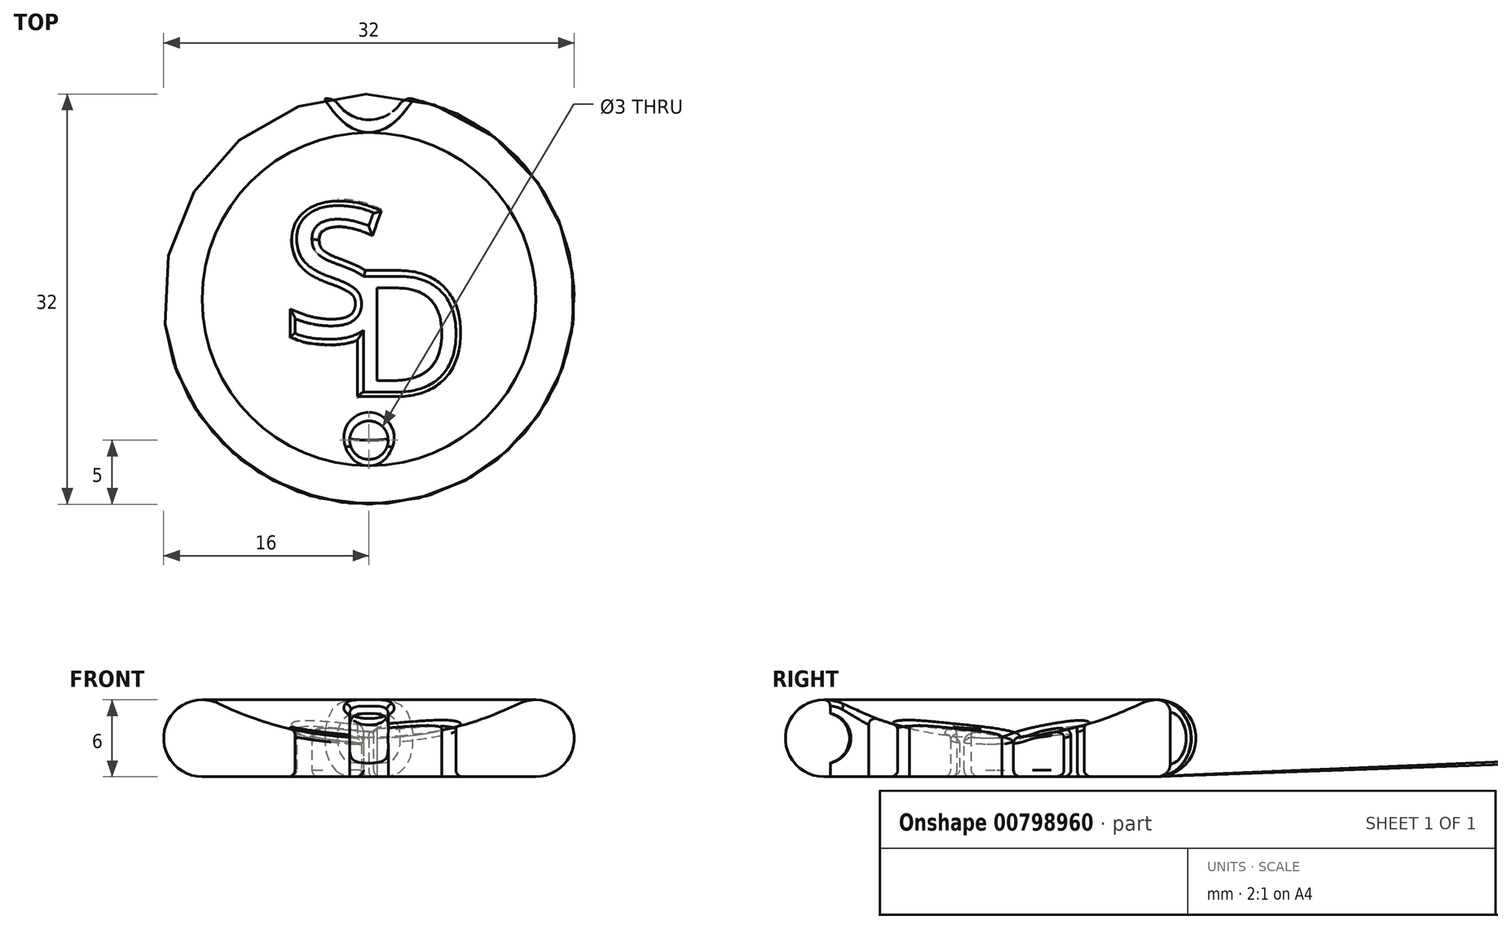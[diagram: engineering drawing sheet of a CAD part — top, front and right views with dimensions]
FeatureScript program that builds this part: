
annotation { "Feature Type Name" : "Feature", "Feature Type Description" : "" }
export const myFeature = defineFeature(function(context is Context, id is Id, definition is map)
    precondition{}
    {
        {
            var Q0;
            Q0=qCreatedBy(makeId("Front.planeOp"),FACE);
            var sketch = newSketch(context, id + "F0", { "sketchPlane" : qUnion([Q0])});
            skArc(sketch, "E0", {"start": v(-11.69, 5.7) * mm, "mid": v(-15.92, 3.67) * mm, "end": v(-13, 0) * mm});
            skArc(sketch, "E1", {"start": v(-11.69, 5.7) * mm, "mid": v(-6, 3.68) * mm, "end": v(0, 3) * mm});
            skLineSegment(sketch, "E2", {"start": v(-13, 0) * mm, "end": v(0, 0) * mm});
            skLineSegment(sketch, "E3", {"start": v(0, 0) * mm, "end": v(0, 3) * mm});
            skSolve(sketch);
        }
        {
            var Q0;
            Q0=makeQuery(id+"F0.imprint","IMPRINT",FACE,{"disambiguationData":[TD([[makeQuery(id+"F0.imprint","IMPRINT",EDGE,{"derivedFrom":sQuery(id+"F0.wireOp",EDGE,"E0")}),1.0]])]});
            var Q1;
            Q1=sQuery(id+"F0.wireOp",EDGE,"E3");
            revolve(context, id + "F1", {"surfaceOperationType" : NewSurfaceOperationType.NEW, "entities" : qUnion([Q0]), "axis" : qUnion([Q1]), "revolveType" : RevolveType.FULL});
        }
        {
            var Q0;
            Q0=qCreatedBy(makeId("Top.planeOp"),FACE);
            var sketch = newSketch(context, id + "F2", { "sketchPlane" : qUnion([Q0])});
            skCircle(sketch, "E4", {"center": v(0, 17) * mm, "radius": 3 * mm});
            skSolve(sketch);
        }
        {
            var Q0;
            Q0=qCreatedBy(makeId("Front.planeOp"),FACE);
            var sketch = newSketch(context, id + "F3", { "sketchPlane" : qUnion([Q0])});
            skCircle(sketch, "E5", {"center": v(-13, 3) * mm, "radius": 2 * mm});
            skSolve(sketch);
        }
        {
            var Q0;
            Q0=qCreatedBy(makeId("Top.planeOp"),FACE);
            var sketch = newSketch(context, id + "F4", { "sketchPlane" : qUnion([Q0])});
            skCircle(sketch, "E6", {"center": v(0, -11) * mm, "radius": 1.5 * mm});
            skSolve(sketch);
        }
        {
            var Q0;
            Q0=qSketchRegion(id+"F4",true);
            extrude(context, id + "F5", {"entities" : qUnion([Q0]), "operationType" : NewBodyOperationType.REMOVE, "depth" : 6 * mm, "offsetDistance" : 25 * mm});
        }
        {
            var Q0;
            Q0=makeQuery(id+"F5.boolean.opBoolean","INTERSECT",EDGE,{"derivedFrom":[makeQuery(id+"F1.opRevolve","SWEPT_FACE",FACE,{"disambiguationData":[OSD([sQuery(id+"F0.wireOp",EDGE,"E1")])]}),makeQuery(id+"F5.opExtrude","SWEPT_FACE",FACE,{"disambiguationData":[OSD([sQuery(id+"F4.wireOp",EDGE,"E6")])]})]});
            var Q1;
            Q1=makeQuery(id+"F5.boolean.opBoolean","INTERSECT",EDGE,{"derivedFrom":[makeQuery(id+"F1.opRevolve","SWEPT_FACE",FACE,{"disambiguationData":[OSD([sQuery(id+"F0.wireOp",EDGE,"E0")])]}),makeQuery(id+"F5.opExtrude","SWEPT_FACE",FACE,{"disambiguationData":[OSD([sQuery(id+"F4.wireOp",EDGE,"E6")])]})]});
            var Q2;
            Q2=makeQuery(id+"F5.boolean.opBoolean","COPY",EDGE,{"derivedFrom":makeQuery(id+"F5.opExtrude","CAP_EDGE",EDGE,{"disambiguationData":[OSD([sQuery(id+"F4.wireOp",EDGE,"E6")])],"isStart":true})});
            fillet(context, id + "F6", {"entities" : qUnion([Q0, Q1, Q2]), "radius" : 0.5 * mm, "tangentPropagation" : true, "allowEdgeOverflow" : false});
        }
        {
            var Q0;
            Q0=qSketchRegion(id+"F3",true);
            var Q1;
            Q1=sQuery(id+"F0.wireOp",EDGE,"E3");
            revolve(context, id + "F7", {"operationType" : NewBodyOperationType.ADD, "surfaceOperationType" : NewSurfaceOperationType.NEW, "entities" : qUnion([Q0]), "axis" : qUnion([Q1]), "revolveType" : RevolveType.FULL});
        }
        {
            var Q0;
            Q0=qSketchRegion(id+"F2",true);
            extrude(context, id + "F8", {"entities" : qUnion([Q0]), "operationType" : NewBodyOperationType.REMOVE, "depth" : 6 * mm, "offsetDistance" : 25 * mm});
        }
        {
            var Q0;
            Q0=makeQuery(id+"F8.boolean.opBoolean","INTERSECT",EDGE,{"derivedFrom":[makeQuery(id+"F1.opRevolve","SWEPT_FACE",FACE,{"disambiguationData":[OSD([sQuery(id+"F0.wireOp",EDGE,"E0")])]}),makeQuery(id+"F8.opExtrude","SWEPT_FACE",FACE,{"disambiguationData":[OSD([sQuery(id+"F2.wireOp",EDGE,"E4")])]})]});
            fillet(context, id + "F9", {"entities" : qUnion([Q0]), "radius" : 1 * mm, "tangentPropagation" : true, "allowEdgeOverflow" : false});
        }
        {
            var Q0;
            Q0=qCreatedBy(makeId("Top.planeOp"),FACE);
            var sketch = newSketch(context, id + "F10", { "sketchPlane" : qUnion([Q0])});
            skText(sketch, "E7", { "text": "S", "fontName": "OpenSans-Regular.ttf"});
            skText(sketch, "E8", { "text": "D", "fontName": "OpenSans-Regular.ttf"});
            const initialGuessF10  = {"E7": [-0.0065, -0.00298, 1, 0, 0.01022], "E8": [-0.00167, -0.00725, 1, 0, 0.00911]};
            skSetInitialGuess(sketch, initialGuessF10);
            skSolve(sketch);
        }
        {
            var Q0;
            Q0=qSketchRegion(id+"F10",true);
            extrude(context, id + "F11", {"entities" : qUnion([Q0]), "operationType" : NewBodyOperationType.REMOVE, "depth" : 6 * mm, "offsetDistance" : 25 * mm});
        }
        {
            var Q0;
            Q0=makeQuery(id+"F11.boolean.opBoolean","INTERSECT",EDGE,{"derivedFrom":[makeQuery(id+"F1.opRevolve","SWEPT_FACE",FACE,{"disambiguationData":[OSD([sQuery(id+"F0.wireOp",EDGE,"E1")])]}),makeQuery(id+"F11.opExtrude","SWEPT_FACE",FACE,{"disambiguationData":[OSD([sQuery(id+"F10.wireOp",EDGE,"E7.sketch_text.stroke-7")])]})]});
            var Q1;
            Q1=makeQuery(id+"F11.boolean.opBoolean","INTERSECT",EDGE,{"derivedFrom":[makeQuery(id+"F1.opRevolve","SWEPT_FACE",FACE,{"disambiguationData":[OSD([sQuery(id+"F0.wireOp",EDGE,"E1")])]}),makeQuery(id+"F11.opExtrude","SWEPT_FACE",FACE,{"disambiguationData":[OSD([sQuery(id+"F10.wireOp",EDGE,"E7.sketch_text.stroke-6")])]})]});
            var Q2;
            Q2=makeQuery(id+"F11.boolean.opBoolean","INTERSECT",EDGE,{"derivedFrom":[makeQuery(id+"F1.opRevolve","SWEPT_FACE",FACE,{"disambiguationData":[OSD([sQuery(id+"F0.wireOp",EDGE,"E1")])]}),makeQuery(id+"F11.opExtrude","SWEPT_FACE",FACE,{"disambiguationData":[OSD([sQuery(id+"F10.wireOp",EDGE,"E7.sketch_text.stroke-4")])]})]});
            var Q3;
            Q3=makeQuery(id+"F11.boolean.opBoolean","INTERSECT",EDGE,{"derivedFrom":[makeQuery(id+"F1.opRevolve","SWEPT_FACE",FACE,{"disambiguationData":[OSD([sQuery(id+"F0.wireOp",EDGE,"E1")])]}),makeQuery(id+"F11.opExtrude","SWEPT_FACE",FACE,{"disambiguationData":[OSD([sQuery(id+"F10.wireOp",EDGE,"E7.sketch_text.stroke-5")])]})]});
            var Q4;
            Q4=makeQuery(id+"F11.boolean.opBoolean","INTERSECT",EDGE,{"derivedFrom":[makeQuery(id+"F1.opRevolve","SWEPT_FACE",FACE,{"disambiguationData":[OSD([sQuery(id+"F0.wireOp",EDGE,"E1")])]}),makeQuery(id+"F11.opExtrude","SWEPT_FACE",FACE,{"disambiguationData":[OSD([sQuery(id+"F10.wireOp",EDGE,"E7.sketch_text.stroke-3")])]})]});
            var Q5;
            Q5=makeQuery(id+"F11.boolean.opBoolean","INTERSECT",EDGE,{"derivedFrom":[makeQuery(id+"F1.opRevolve","SWEPT_FACE",FACE,{"disambiguationData":[OSD([sQuery(id+"F0.wireOp",EDGE,"E1")])]}),makeQuery(id+"F11.opExtrude","SWEPT_FACE",FACE,{"disambiguationData":[OSD([sQuery(id+"F10.wireOp",EDGE,"E7.sketch_text.stroke-2")])]})]});
            var Q6;
            Q6=makeQuery(id+"F11.boolean.opBoolean","INTERSECT",EDGE,{"derivedFrom":[makeQuery(id+"F1.opRevolve","SWEPT_FACE",FACE,{"disambiguationData":[OSD([sQuery(id+"F0.wireOp",EDGE,"E1")])]}),makeQuery(id+"F11.opExtrude","SWEPT_FACE",FACE,{"disambiguationData":[OSD([sQuery(id+"F10.wireOp",EDGE,"E7.sketch_text.stroke-1")])]})]});
            var Q7;
            Q7=makeQuery(id+"F11.boolean.opBoolean","INTERSECT",EDGE,{"derivedFrom":[makeQuery(id+"F1.opRevolve","SWEPT_FACE",FACE,{"disambiguationData":[OSD([sQuery(id+"F0.wireOp",EDGE,"E1")])]}),makeQuery(id+"F11.opExtrude","SWEPT_FACE",FACE,{"disambiguationData":[OSD([sQuery(id+"F10.wireOp",EDGE,"E8.sketch_text.stroke-3")])]})]});
            var Q8;
            Q8=makeQuery(id+"F11.boolean.opBoolean","INTERSECT",EDGE,{"derivedFrom":[makeQuery(id+"F1.opRevolve","SWEPT_FACE",FACE,{"disambiguationData":[OSD([sQuery(id+"F0.wireOp",EDGE,"E1")])]}),makeQuery(id+"F11.opExtrude","SWEPT_FACE",FACE,{"disambiguationData":[OSD([sQuery(id+"F10.wireOp",EDGE,"E8.sketch_text.stroke-2")])]})]});
            var Q9;
            Q9=makeQuery(id+"F11.boolean.opBoolean","INTERSECT",EDGE,{"derivedFrom":[makeQuery(id+"F1.opRevolve","SWEPT_FACE",FACE,{"disambiguationData":[OSD([sQuery(id+"F0.wireOp",EDGE,"E1")])]}),makeQuery(id+"F11.opExtrude","SWEPT_FACE",FACE,{"disambiguationData":[OSD([sQuery(id+"F10.wireOp",EDGE,"E8.sketch_text.stroke-1")])]})]});
            var Q10;
            Q10=makeQuery(id+"F11.boolean.opBoolean","INTERSECT",EDGE,{"derivedFrom":[makeQuery(id+"F1.opRevolve","SWEPT_FACE",FACE,{"disambiguationData":[OSD([sQuery(id+"F0.wireOp",EDGE,"E1")])]}),makeQuery(id+"F11.opExtrude","SWEPT_FACE",FACE,{"disambiguationData":[OSD([sQuery(id+"F10.wireOp",EDGE,"E8.sketch_text.stroke-0")])]})]});
            var Q11;
            Q11=makeQuery(id+"F11.boolean.opBoolean","INTERSECT",EDGE,{"derivedFrom":[makeQuery(id+"F1.opRevolve","SWEPT_FACE",FACE,{"disambiguationData":[OSD([sQuery(id+"F0.wireOp",EDGE,"E1")])]}),makeQuery(id+"F11.opExtrude","SWEPT_FACE",FACE,{"disambiguationData":[OSD([sQuery(id+"F10.wireOp",EDGE,"E8.sketch_text.stroke-6")])]})]});
            var Q12;
            Q12=makeQuery(id+"F11.boolean.opBoolean","INTERSECT",EDGE,{"derivedFrom":[makeQuery(id+"F1.opRevolve","SWEPT_FACE",FACE,{"disambiguationData":[OSD([sQuery(id+"F0.wireOp",EDGE,"E1")])]}),makeQuery(id+"F11.opExtrude","SWEPT_FACE",FACE,{"disambiguationData":[OSD([sQuery(id+"F10.wireOp",EDGE,"E8.sketch_text.stroke-5")])]})]});
            var Q13;
            Q13=makeQuery(id+"F11.boolean.opBoolean","INTERSECT",EDGE,{"derivedFrom":[makeQuery(id+"F1.opRevolve","SWEPT_FACE",FACE,{"disambiguationData":[OSD([sQuery(id+"F0.wireOp",EDGE,"E1")])]}),makeQuery(id+"F11.opExtrude","SWEPT_FACE",FACE,{"disambiguationData":[OSD([sQuery(id+"F10.wireOp",EDGE,"E8.sketch_text.stroke-4")])]})]});
            var Q14;
            Q14=makeQuery(id+"F11.boolean.opBoolean","INTERSECT",EDGE,{"derivedFrom":[makeQuery(id+"F1.opRevolve","SWEPT_FACE",FACE,{"disambiguationData":[OSD([sQuery(id+"F0.wireOp",EDGE,"E1")])]}),makeQuery(id+"F11.opExtrude","SWEPT_FACE",FACE,{"disambiguationData":[OSD([sQuery(id+"F10.wireOp",EDGE,"E7.sketch_text.stroke-24")])]})]});
            var Q15;
            Q15=makeQuery(id+"F11.boolean.opBoolean","INTERSECT",EDGE,{"derivedFrom":[makeQuery(id+"F1.opRevolve","SWEPT_FACE",FACE,{"disambiguationData":[OSD([sQuery(id+"F0.wireOp",EDGE,"E1")])]}),makeQuery(id+"F11.opExtrude","SWEPT_FACE",FACE,{"disambiguationData":[OSD([sQuery(id+"F10.wireOp",EDGE,"E7.sketch_text.stroke-23")])]})]});
            var Q16;
            Q16=makeQuery(id+"F11.boolean.opBoolean","INTERSECT",EDGE,{"derivedFrom":[makeQuery(id+"F1.opRevolve","SWEPT_FACE",FACE,{"disambiguationData":[OSD([sQuery(id+"F0.wireOp",EDGE,"E1")])]}),makeQuery(id+"F11.opExtrude","SWEPT_FACE",FACE,{"disambiguationData":[OSD([sQuery(id+"F10.wireOp",EDGE,"E7.sketch_text.stroke-22")])]})]});
            var Q17;
            Q17=makeQuery(id+"F11.boolean.opBoolean","INTERSECT",EDGE,{"derivedFrom":[makeQuery(id+"F1.opRevolve","SWEPT_FACE",FACE,{"disambiguationData":[OSD([sQuery(id+"F0.wireOp",EDGE,"E1")])]}),makeQuery(id+"F11.opExtrude","SWEPT_FACE",FACE,{"disambiguationData":[OSD([sQuery(id+"F10.wireOp",EDGE,"E7.sketch_text.stroke-21")])]})]});
            var Q18;
            Q18=makeQuery(id+"F11.boolean.opBoolean","INTERSECT",EDGE,{"derivedFrom":[makeQuery(id+"F1.opRevolve","SWEPT_FACE",FACE,{"disambiguationData":[OSD([sQuery(id+"F0.wireOp",EDGE,"E1")])]}),makeQuery(id+"F11.opExtrude","SWEPT_FACE",FACE,{"disambiguationData":[OSD([sQuery(id+"F10.wireOp",EDGE,"E7.sketch_text.stroke-20")])]})]});
            var Q19;
            Q19=makeQuery(id+"F11.boolean.opBoolean","INTERSECT",EDGE,{"derivedFrom":[makeQuery(id+"F1.opRevolve","SWEPT_FACE",FACE,{"disambiguationData":[OSD([sQuery(id+"F0.wireOp",EDGE,"E1")])]}),makeQuery(id+"F11.opExtrude","SWEPT_FACE",FACE,{"disambiguationData":[OSD([sQuery(id+"F10.wireOp",EDGE,"E7.sketch_text.stroke-19")])]})]});
            var Q20;
            Q20=makeQuery(id+"F11.boolean.opBoolean","INTERSECT",EDGE,{"derivedFrom":[makeQuery(id+"F1.opRevolve","SWEPT_FACE",FACE,{"disambiguationData":[OSD([sQuery(id+"F0.wireOp",EDGE,"E1")])]}),makeQuery(id+"F11.opExtrude","SWEPT_FACE",FACE,{"disambiguationData":[OSD([sQuery(id+"F10.wireOp",EDGE,"E7.sketch_text.stroke-18")])]})]});
            var Q21;
            Q21=makeQuery(id+"F11.boolean.opBoolean","INTERSECT",EDGE,{"derivedFrom":[makeQuery(id+"F1.opRevolve","SWEPT_FACE",FACE,{"disambiguationData":[OSD([sQuery(id+"F0.wireOp",EDGE,"E1")])]}),makeQuery(id+"F11.opExtrude","SWEPT_FACE",FACE,{"disambiguationData":[OSD([sQuery(id+"F10.wireOp",EDGE,"E7.sketch_text.stroke-17")])]})]});
            var Q22;
            Q22=makeQuery(id+"F11.boolean.opBoolean","INTERSECT",EDGE,{"derivedFrom":[makeQuery(id+"F1.opRevolve","SWEPT_FACE",FACE,{"disambiguationData":[OSD([sQuery(id+"F0.wireOp",EDGE,"E1")])]}),makeQuery(id+"F11.opExtrude","SWEPT_FACE",FACE,{"disambiguationData":[OSD([sQuery(id+"F10.wireOp",EDGE,"E7.sketch_text.stroke-16")])]})]});
            var Q23;
            Q23=makeQuery(id+"F11.boolean.opBoolean","INTERSECT",EDGE,{"derivedFrom":[makeQuery(id+"F1.opRevolve","SWEPT_FACE",FACE,{"disambiguationData":[OSD([sQuery(id+"F0.wireOp",EDGE,"E1")])]}),makeQuery(id+"F11.opExtrude","SWEPT_FACE",FACE,{"disambiguationData":[OSD([sQuery(id+"F10.wireOp",EDGE,"E7.sketch_text.stroke-15")])]})]});
            var Q24;
            Q24=makeQuery(id+"F11.boolean.opBoolean","INTERSECT",EDGE,{"derivedFrom":[makeQuery(id+"F1.opRevolve","SWEPT_FACE",FACE,{"disambiguationData":[OSD([sQuery(id+"F0.wireOp",EDGE,"E1")])]}),makeQuery(id+"F11.opExtrude","SWEPT_FACE",FACE,{"disambiguationData":[OSD([sQuery(id+"F10.wireOp",EDGE,"E7.sketch_text.stroke-14")])]})]});
            var Q25;
            Q25=makeQuery(id+"F11.boolean.opBoolean","INTERSECT",EDGE,{"derivedFrom":[makeQuery(id+"F1.opRevolve","SWEPT_FACE",FACE,{"disambiguationData":[OSD([sQuery(id+"F0.wireOp",EDGE,"E1")])]}),makeQuery(id+"F11.opExtrude","SWEPT_FACE",FACE,{"disambiguationData":[OSD([sQuery(id+"F10.wireOp",EDGE,"E7.sketch_text.stroke-13")])]})]});
            var Q26;
            Q26=makeQuery(id+"F11.boolean.opBoolean","INTERSECT",EDGE,{"derivedFrom":[makeQuery(id+"F1.opRevolve","SWEPT_FACE",FACE,{"disambiguationData":[OSD([sQuery(id+"F0.wireOp",EDGE,"E1")])]}),makeQuery(id+"F11.opExtrude","SWEPT_FACE",FACE,{"disambiguationData":[OSD([sQuery(id+"F10.wireOp",EDGE,"E7.sketch_text.stroke-12")])]})]});
            var Q27;
            Q27=makeQuery(id+"F11.boolean.opBoolean","INTERSECT",EDGE,{"derivedFrom":[makeQuery(id+"F1.opRevolve","SWEPT_FACE",FACE,{"disambiguationData":[OSD([sQuery(id+"F0.wireOp",EDGE,"E1")])]}),makeQuery(id+"F11.opExtrude","SWEPT_FACE",FACE,{"disambiguationData":[OSD([sQuery(id+"F10.wireOp",EDGE,"E7.sketch_text.stroke-11")])]})]});
            var Q28;
            Q28=makeQuery(id+"F11.boolean.opBoolean","INTERSECT",EDGE,{"derivedFrom":[makeQuery(id+"F1.opRevolve","SWEPT_FACE",FACE,{"disambiguationData":[OSD([sQuery(id+"F0.wireOp",EDGE,"E1")])]}),makeQuery(id+"F11.opExtrude","SWEPT_FACE",FACE,{"disambiguationData":[OSD([sQuery(id+"F10.wireOp",EDGE,"E7.sketch_text.stroke-10")])]})]});
            var Q29;
            Q29=makeQuery(id+"F11.boolean.opBoolean","INTERSECT",EDGE,{"derivedFrom":[makeQuery(id+"F1.opRevolve","SWEPT_FACE",FACE,{"disambiguationData":[OSD([sQuery(id+"F0.wireOp",EDGE,"E1")])]}),makeQuery(id+"F11.opExtrude","SWEPT_FACE",FACE,{"disambiguationData":[OSD([sQuery(id+"F10.wireOp",EDGE,"E7.sketch_text.stroke-9")])]})]});
            var Q30;
            Q30=makeQuery(id+"F11.boolean.opBoolean","INTERSECT",EDGE,{"derivedFrom":[makeQuery(id+"F1.opRevolve","SWEPT_FACE",FACE,{"disambiguationData":[OSD([sQuery(id+"F0.wireOp",EDGE,"E1")])]}),makeQuery(id+"F11.opExtrude","SWEPT_FACE",FACE,{"disambiguationData":[OSD([sQuery(id+"F10.wireOp",EDGE,"E7.sketch_text.stroke-8")])]})]});
            var Q31;
            Q31=makeQuery(id+"F11.boolean.opBoolean","COPY",EDGE,{"derivedFrom":makeQuery(id+"F11.opExtrude","CAP_EDGE",EDGE,{"disambiguationData":[OSD([sQuery(id+"F10.wireOp",EDGE,"E8.sketch_text.stroke-3")])],"isStart":true})});
            var Q32;
            Q32=makeQuery(id+"F11.boolean.opBoolean","COPY",EDGE,{"derivedFrom":makeQuery(id+"F11.opExtrude","CAP_EDGE",EDGE,{"disambiguationData":[OSD([sQuery(id+"F10.wireOp",EDGE,"E8.sketch_text.stroke-2")])],"isStart":true})});
            var Q33;
            Q33=makeQuery(id+"F11.boolean.opBoolean","COPY",EDGE,{"derivedFrom":makeQuery(id+"F11.opExtrude","CAP_EDGE",EDGE,{"disambiguationData":[OSD([sQuery(id+"F10.wireOp",EDGE,"E8.sketch_text.stroke-0")])],"isStart":true})});
            var Q34;
            Q34=makeQuery(id+"F11.boolean.opBoolean","COPY",EDGE,{"derivedFrom":makeQuery(id+"F11.opExtrude","CAP_EDGE",EDGE,{"disambiguationData":[OSD([sQuery(id+"F10.wireOp",EDGE,"E8.sketch_text.stroke-1")])],"isStart":true})});
            var Q35;
            Q35=makeQuery(id+"F11.boolean.opBoolean","COPY",EDGE,{"derivedFrom":makeQuery(id+"F11.opExtrude","CAP_EDGE",EDGE,{"disambiguationData":[OSD([sQuery(id+"F10.wireOp",EDGE,"E8.sketch_text.stroke-6")])],"isStart":true})});
            var Q36;
            Q36=makeQuery(id+"F11.boolean.opBoolean","COPY",EDGE,{"derivedFrom":makeQuery(id+"F11.opExtrude","CAP_EDGE",EDGE,{"disambiguationData":[OSD([sQuery(id+"F10.wireOp",EDGE,"E8.sketch_text.stroke-5")])],"isStart":true})});
            var Q37;
            Q37=makeQuery(id+"F11.boolean.opBoolean","COPY",EDGE,{"derivedFrom":makeQuery(id+"F11.opExtrude","CAP_EDGE",EDGE,{"disambiguationData":[OSD([sQuery(id+"F10.wireOp",EDGE,"E8.sketch_text.stroke-4")])],"isStart":true})});
            var Q38;
            Q38=makeQuery(id+"F11.boolean.opBoolean","COPY",EDGE,{"derivedFrom":makeQuery(id+"F11.opExtrude","CAP_EDGE",EDGE,{"disambiguationData":[OSD([sQuery(id+"F10.wireOp",EDGE,"E7.sketch_text.stroke-24")])],"isStart":true})});
            var Q39;
            Q39=makeQuery(id+"F11.boolean.opBoolean","COPY",EDGE,{"derivedFrom":makeQuery(id+"F11.opExtrude","CAP_EDGE",EDGE,{"disambiguationData":[OSD([sQuery(id+"F10.wireOp",EDGE,"E7.sketch_text.stroke-23")])],"isStart":true})});
            var Q40;
            Q40=makeQuery(id+"F11.boolean.opBoolean","COPY",EDGE,{"derivedFrom":makeQuery(id+"F11.opExtrude","CAP_EDGE",EDGE,{"disambiguationData":[OSD([sQuery(id+"F10.wireOp",EDGE,"E7.sketch_text.stroke-22")])],"isStart":true})});
            var Q41;
            Q41=makeQuery(id+"F11.boolean.opBoolean","COPY",EDGE,{"derivedFrom":makeQuery(id+"F11.opExtrude","CAP_EDGE",EDGE,{"disambiguationData":[OSD([sQuery(id+"F10.wireOp",EDGE,"E7.sketch_text.stroke-20")])],"isStart":true})});
            var Q42;
            Q42=makeQuery(id+"F11.boolean.opBoolean","COPY",EDGE,{"derivedFrom":makeQuery(id+"F11.opExtrude","CAP_EDGE",EDGE,{"disambiguationData":[OSD([sQuery(id+"F10.wireOp",EDGE,"E7.sketch_text.stroke-19")])],"isStart":true})});
            var Q43;
            Q43=makeQuery(id+"F11.boolean.opBoolean","COPY",EDGE,{"derivedFrom":makeQuery(id+"F11.opExtrude","CAP_EDGE",EDGE,{"disambiguationData":[OSD([sQuery(id+"F10.wireOp",EDGE,"E7.sketch_text.stroke-18")])],"isStart":true})});
            var Q44;
            Q44=makeQuery(id+"F11.boolean.opBoolean","COPY",EDGE,{"derivedFrom":makeQuery(id+"F11.opExtrude","CAP_EDGE",EDGE,{"disambiguationData":[OSD([sQuery(id+"F10.wireOp",EDGE,"E7.sketch_text.stroke-17")])],"isStart":true})});
            var Q45;
            Q45=makeQuery(id+"F11.boolean.opBoolean","COPY",EDGE,{"derivedFrom":makeQuery(id+"F11.opExtrude","CAP_EDGE",EDGE,{"disambiguationData":[OSD([sQuery(id+"F10.wireOp",EDGE,"E7.sketch_text.stroke-16")])],"isStart":true})});
            var Q46;
            Q46=makeQuery(id+"F11.boolean.opBoolean","COPY",EDGE,{"derivedFrom":makeQuery(id+"F11.opExtrude","CAP_EDGE",EDGE,{"disambiguationData":[OSD([sQuery(id+"F10.wireOp",EDGE,"E7.sketch_text.stroke-15")])],"isStart":true})});
            var Q47;
            Q47=makeQuery(id+"F11.boolean.opBoolean","COPY",EDGE,{"derivedFrom":makeQuery(id+"F11.opExtrude","CAP_EDGE",EDGE,{"disambiguationData":[OSD([sQuery(id+"F10.wireOp",EDGE,"E7.sketch_text.stroke-14")])],"isStart":true})});
            var Q48;
            Q48=makeQuery(id+"F11.boolean.opBoolean","COPY",EDGE,{"derivedFrom":makeQuery(id+"F11.opExtrude","CAP_EDGE",EDGE,{"disambiguationData":[OSD([sQuery(id+"F10.wireOp",EDGE,"E7.sketch_text.stroke-13")])],"isStart":true})});
            var Q49;
            Q49=makeQuery(id+"F11.boolean.opBoolean","COPY",EDGE,{"derivedFrom":makeQuery(id+"F11.opExtrude","CAP_EDGE",EDGE,{"disambiguationData":[OSD([sQuery(id+"F10.wireOp",EDGE,"E7.sketch_text.stroke-12")])],"isStart":true})});
            var Q50;
            Q50=makeQuery(id+"F11.boolean.opBoolean","COPY",EDGE,{"derivedFrom":makeQuery(id+"F11.opExtrude","CAP_EDGE",EDGE,{"disambiguationData":[OSD([sQuery(id+"F10.wireOp",EDGE,"E7.sketch_text.stroke-11")])],"isStart":true})});
            var Q51;
            Q51=makeQuery(id+"F11.boolean.opBoolean","COPY",EDGE,{"derivedFrom":makeQuery(id+"F11.opExtrude","CAP_EDGE",EDGE,{"disambiguationData":[OSD([sQuery(id+"F10.wireOp",EDGE,"E7.sketch_text.stroke-10")])],"isStart":true})});
            var Q52;
            Q52=makeQuery(id+"F11.boolean.opBoolean","COPY",EDGE,{"derivedFrom":makeQuery(id+"F11.opExtrude","CAP_EDGE",EDGE,{"disambiguationData":[OSD([sQuery(id+"F10.wireOp",EDGE,"E7.sketch_text.stroke-9")])],"isStart":true})});
            var Q53;
            Q53=makeQuery(id+"F11.boolean.opBoolean","COPY",EDGE,{"derivedFrom":makeQuery(id+"F11.opExtrude","CAP_EDGE",EDGE,{"disambiguationData":[OSD([sQuery(id+"F10.wireOp",EDGE,"E7.sketch_text.stroke-8")])],"isStart":true})});
            var Q54;
            Q54=makeQuery(id+"F11.boolean.opBoolean","COPY",EDGE,{"derivedFrom":makeQuery(id+"F11.opExtrude","CAP_EDGE",EDGE,{"disambiguationData":[OSD([sQuery(id+"F10.wireOp",EDGE,"E7.sketch_text.stroke-7")])],"isStart":true})});
            var Q55;
            Q55=makeQuery(id+"F11.boolean.opBoolean","COPY",EDGE,{"derivedFrom":makeQuery(id+"F11.opExtrude","CAP_EDGE",EDGE,{"disambiguationData":[OSD([sQuery(id+"F10.wireOp",EDGE,"E7.sketch_text.stroke-6")])],"isStart":true})});
            var Q56;
            Q56=makeQuery(id+"F11.boolean.opBoolean","COPY",EDGE,{"derivedFrom":makeQuery(id+"F11.opExtrude","CAP_EDGE",EDGE,{"disambiguationData":[OSD([sQuery(id+"F10.wireOp",EDGE,"E7.sketch_text.stroke-5")])],"isStart":true})});
            var Q57;
            Q57=makeQuery(id+"F11.boolean.opBoolean","COPY",EDGE,{"derivedFrom":makeQuery(id+"F11.opExtrude","CAP_EDGE",EDGE,{"disambiguationData":[OSD([sQuery(id+"F10.wireOp",EDGE,"E7.sketch_text.stroke-4")])],"isStart":true})});
            var Q58;
            Q58=makeQuery(id+"F11.boolean.opBoolean","COPY",EDGE,{"derivedFrom":makeQuery(id+"F11.opExtrude","CAP_EDGE",EDGE,{"disambiguationData":[OSD([sQuery(id+"F10.wireOp",EDGE,"E7.sketch_text.stroke-3")])],"isStart":true})});
            var Q59;
            Q59=makeQuery(id+"F11.boolean.opBoolean","COPY",EDGE,{"derivedFrom":makeQuery(id+"F11.opExtrude","CAP_EDGE",EDGE,{"disambiguationData":[OSD([sQuery(id+"F10.wireOp",EDGE,"E7.sketch_text.stroke-2")])],"isStart":true})});
            var Q60;
            Q60=makeQuery(id+"F11.boolean.opBoolean","COPY",EDGE,{"derivedFrom":makeQuery(id+"F11.opExtrude","CAP_EDGE",EDGE,{"disambiguationData":[OSD([sQuery(id+"F10.wireOp",EDGE,"E7.sketch_text.stroke-1")])],"isStart":true})});
            fillet(context, id + "F12", {"entities" : qUnion([Q0, Q1, Q2, Q3, Q4, Q5, Q6, Q7, Q8, Q9, Q10, Q11, Q12, Q13, Q14, Q15, Q16, Q17, Q18, Q19, Q20, Q21, Q22, Q23, Q24, Q25, Q26, Q27, Q28, Q29, Q30, Q31, Q32, Q33, Q34, Q35, Q36, Q37, Q38, Q39, Q40, Q41, Q42, Q43, Q44, Q45, Q46, Q47, Q48, Q49, Q50, Q51, Q52, Q53, Q54, Q55, Q56, Q57, Q58, Q59, Q60]), "radius" : 0.5 * mm, "tangentPropagation" : true, "allowEdgeOverflow" : false});
        }
    });
